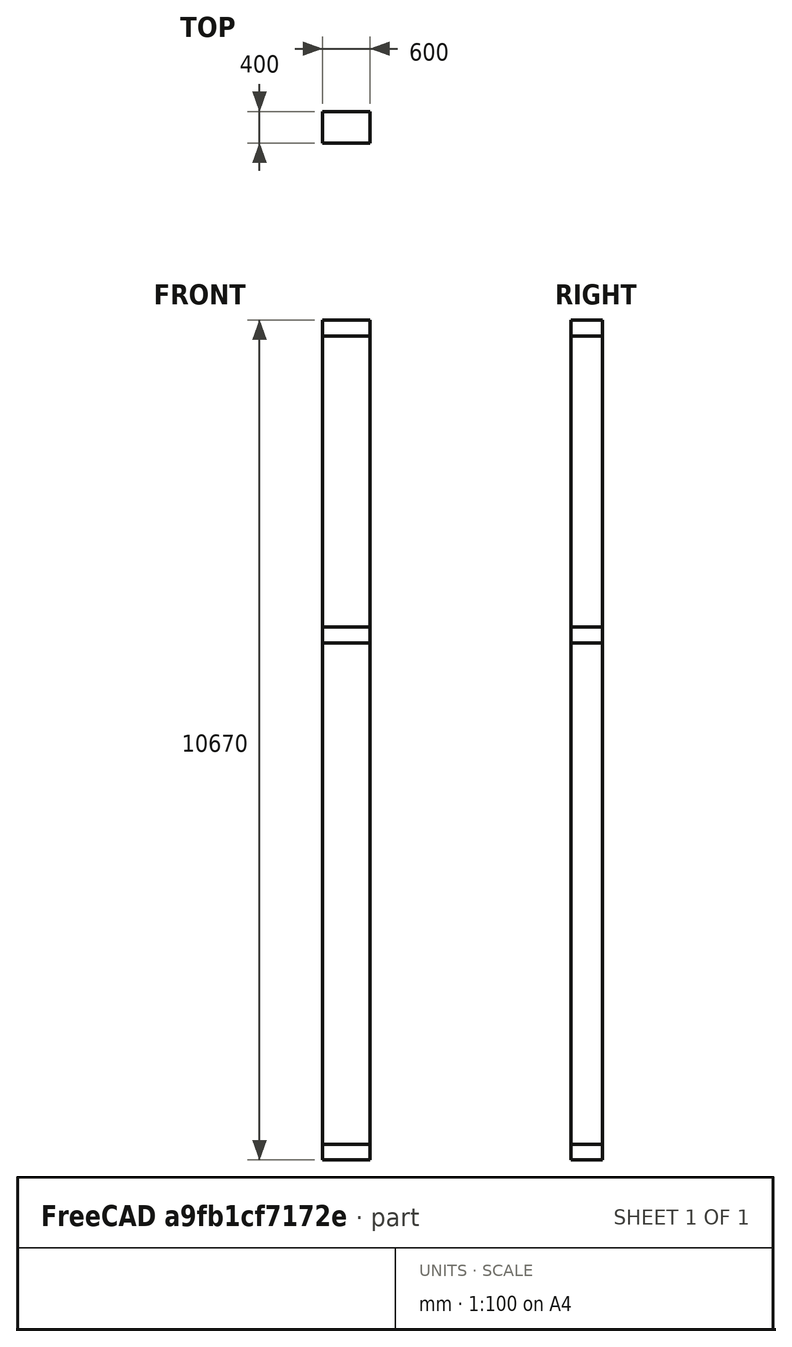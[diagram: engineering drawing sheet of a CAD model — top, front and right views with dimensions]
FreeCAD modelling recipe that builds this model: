
FCSTD DOCUMENT  (FreeCAD 0.21R33694 (Git))
Label: column
License: All rights reserved
LicenseURL: http://en.wikipedia.org/wiki/All_rights_reserved
objects: Part::FeaturePython×7, Part::Plane×5, Fem::ConstraintDisplacement×5, Part::Feature×5, Fem::ConstraintForce×4, Fem::FemSolverObjectPython×1, App::MaterialObjectPython×1, Part::Box×1, Fem::FemMeshObjectPython×1, Fem::FemAnalysis×1
note: 18 computed .brp shape members not serialized (recipe doc carries the construction recipe); baked Part::Feature solids carry a one-line shape summary decoded from their .brp

FEATURE [Fem::FemSolverObjectPython] SolverCcxTools  # FEM object (typed FeaturePython)
  AnalysisType = 0
  BeamShellResultOutput3D = true
  BucklingFactors = 1
  EigenmodeHighLimit = 1000000
  EigenmodeLowLimit = 0
  EigenmodesCount = 10
  GeometricalNonlinearity = 0
  IterationsControlParameterCutb = 0.25,0.5,0.75,0.85,,,1.5,
  IterationsControlParameterIter = 4,8,9,200,10,400,,200,,
  IterationsControlParameterTimeUse = false
  IterationsThermoMechMaximum = 2000
  IterationsUserDefinedIncrementations = false
  IterationsUserDefinedTimeStepLength = false
  MaterialNonlinearity = 0
  MatrixSolverType = 0
  SplitInputWriter = true
  ThermoMechSteadyState = true
  TimeEnd = 1
  TimeInitialStep = 0.01
FEATURE [App::MaterialObjectPython] MaterialSolid  label="B450"  # material (typed FeaturePython)
  Category = 0
  Material = AngleOfFriction=30 deg,AuthorAndLicense=(c) 2019 Bernd Hahnebach (CC-BY 3.0),CardName=Concrete-EN-C35_45,CompressiveStrength=15.75 MPa,+7 more (map truncated)
FEATURE [Part::Box] Box  label="Cube"
  AttacherType = Attacher::AttachEngine3D
  Height = 10670
  Length = 600
  Width = 400
FEATURE [Part::Plane] Plane
  AttacherType = Attacher::AttachEngine3D
  Length = 600
  Width = 400
FEATURE [Part::Plane] Plane001
  AttacherType = Attacher::AttachEngine3D
  Length = 600
  Placement = pos=(0,0,200) rot=(0,0,1;0rad)
  Width = 400
FEATURE [Part::Plane] Plane002
  AttacherType = Attacher::AttachEngine3D
  Length = 600
  Placement = pos=(0,0,6570) rot=(0,0,1;0rad)
  Width = 400
FEATURE [Part::Plane] Plane003
  AttacherType = Attacher::AttachEngine3D
  Length = 600
  Placement = pos=(0,0,6770) rot=(0,0,1;0rad)
  Width = 400
FEATURE [Part::Plane] Plane004
  AttacherType = Attacher::AttachEngine3D
  Length = 600
  Placement = pos=(0,0,10470) rot=(0,0,1;0rad)
  Width = 400
FEATURE [Part::FeaturePython] Slice  # WARN: FeaturePython — macro-defined, semantics opaque (R4)
  Base = -> Box
  Mode = 1
  Tolerance = 0
  Tools = -> [Plane,Plane001,Plane002,Plane003,Plane004]
FEATURE [Part::FeaturePython] Slice_child0  label="Slice.0"  # WARN: FeaturePython — macro-defined, semantics opaque (R4)
  Base = -> Slice
  FilterType = 1
  Invert = false
  OverrideMaxVal = 0
  WindowFrom = 80
  WindowTo = 100
  items = 0
FEATURE [Part::FeaturePython] Slice_child1  label="Slice.1"  # WARN: FeaturePython — macro-defined, semantics opaque (R4)
  Base = -> Slice
  FilterType = 1
  Invert = false
  OverrideMaxVal = 0
  WindowFrom = 80
  WindowTo = 100
  items = 1
FEATURE [Part::FeaturePython] Slice_child2  label="Slice.2"  # WARN: FeaturePython — macro-defined, semantics opaque (R4)
  Base = -> Slice
  FilterType = 1
  Invert = false
  OverrideMaxVal = 0
  WindowFrom = 80
  WindowTo = 100
  items = 2
FEATURE [Part::FeaturePython] Slice_child3  label="Slice.3"  # WARN: FeaturePython — macro-defined, semantics opaque (R4)
  Base = -> Slice
  FilterType = 1
  Invert = false
  OverrideMaxVal = 0
  WindowFrom = 80
  WindowTo = 100
  items = 3
FEATURE [Part::FeaturePython] Slice_child4  label="Slice.4"  # WARN: FeaturePython — macro-defined, semantics opaque (R4)
  Base = -> Slice
  FilterType = 1
  Invert = false
  OverrideMaxVal = 0
  WindowFrom = 80
  WindowTo = 100
  items = 4
FEATURE [Fem::ConstraintForce] ConstraintForce  label="wind"
  DirectionVector = (1,0,0)
  Force = 42000
  NormalDirection = (-1,0,0)
  Points = (136) [(0,400,0),(0,400,66.6667),(0,400,133.333),(0,400,200),(0,266.667,0),(0,266.667,66.6667),(0,266.667,133.333),(0,266.667,200),(0,133.333,0),+127 more]
  References = -> [Slice_child0,Slice_child1,Slice_child2,Slice_child3,Slice_child4]
  Reversed = true
  Scale = 19
FEATURE [Fem::ConstraintForce] ConstraintForce001  label="mast"
  DirectionVector = (1,0,0)
  Force = 10000
  NormalDirection = (-1,0,0)
  Points = (16) [(0,400,6570),(0,400,6636.67),(0,400,6703.33),(0,400,6770),(0,266.667,6570),(0,266.667,6636.67),(0,266.667,6703.33),(0,266.667,6770),(0,133.333,6570),+7 more]
  References = -> [Slice_child2]
  Reversed = true
  Scale = 19
FEATURE [Fem::ConstraintForce] ConstraintForce002  label="beam(p)"
  DirectionVector = (0,0,-1)
  Force = 100000
  NormalDirection = (0,0,1)
  Points = (16) [(0,0,10670),(200,0,10670),(400,0,10670),(600,0,10670),(0,133.333,10670),(200,133.333,10670),(400,133.333,10670),(600,133.333,10670),(0,266.667,10670),+7 more]
  References = -> [Slice_child4]
  Reversed = true
  Scale = 24
FEATURE [Fem::ConstraintDisplacement] ConstraintDisplacement  label="top_x"
  NormalDirection = (0,0,1)
  Normals = (4) [(0,0,1),(0,0,1),(0,0,1),(0,0,1)]
  Points = (4) [(600,0,10670),(600,133.333,10670),(600,266.667,10670),(600,400,10670)]
  References = -> [Slice_child4]
  Scale = 22
  hasXFormula = false
  hasYFormula = false
  hasZFormula = false
  rotxFix = false
  rotxFree = true
  rotyFix = false
  rotyFree = true
  rotzFix = false
  rotzFree = true
  useFlowSurfaceForce = false
  xDisplacement = 0
  xFix = false
  xFree = false
  xRotation = 0
  yDisplacement = 0
  yFix = false
  yFree = false
  yRotation = 0
  zDisplacement = 0
  zFix = false
  zFree = true
  zRotation = 0
FEATURE [Fem::ConstraintDisplacement] ConstraintDisplacement001  label="bottom_x"
  NormalDirection = (0,0,1)
  Normals = (4) [(0,0,1),(0,0,1),(0,0,1),(0,0,1)]
  Points = (4) [(600,0,0),(600,133.333,0),(600,266.667,0),(600,400,0)]
  References = -> [Slice_child0]
  Scale = 22
  hasXFormula = false
  hasYFormula = false
  hasZFormula = false
  rotxFix = false
  rotxFree = true
  rotyFix = false
  rotyFree = true
  rotzFix = false
  rotzFree = true
  useFlowSurfaceForce = false
  xDisplacement = 0
  xFix = false
  xFree = false
  xRotation = 0
  yDisplacement = 0
  yFix = false
  yFree = true
  yRotation = 0
  zDisplacement = 0
  zFix = false
  zFree = true
  zRotation = 0
FEATURE [Fem::ConstraintDisplacement] ConstraintDisplacement002  label="bottom_y"
  NormalDirection = (0,0,1)
  Normals = (4) [(0,0,1),(0,0,1),(0,0,1),(0,0,1)]
  Points = (4) [(0,0,0),(200,0,0),(400,0,0),(600,0,0)]
  References = -> [Slice_child0]
  Scale = 26
  hasXFormula = false
  hasYFormula = false
  hasZFormula = false
  rotxFix = false
  rotxFree = true
  rotyFix = false
  rotyFree = true
  rotzFix = false
  rotzFree = true
  useFlowSurfaceForce = false
  xDisplacement = 0
  xFix = false
  xFree = true
  xRotation = 0
  yDisplacement = 0
  yFix = false
  yFree = false
  yRotation = 0
  zDisplacement = 0
  zFix = false
  zFree = true
  zRotation = 0
FEATURE [Fem::ConstraintDisplacement] ConstraintDisplacement003  label="bottom_z"
  NormalDirection = (0,0,-1)
  Normals = (4) [(0,0,-1),(0,0,-1),(0,0,-1),(0,0,-1)]
  Points = (4) [(600,0,0),(600,133.333,0),(600,266.667,0),(600,400,0)]
  References = -> [Slice_child0]
  Scale = 22
  hasXFormula = false
  hasYFormula = false
  hasZFormula = false
  rotxFix = false
  rotxFree = true
  rotyFix = false
  rotyFree = true
  rotzFix = false
  rotzFree = true
  useFlowSurfaceForce = false
  xDisplacement = 0
  xFix = false
  xFree = true
  xRotation = 0
  yDisplacement = 0
  yFix = false
  yFree = true
  yRotation = 0
  zDisplacement = 0
  zFix = false
  zFree = false
  zRotation = 0
FEATURE [Fem::ConstraintDisplacement] ConstraintDisplacement004  label="top_y"
  NormalDirection = (0,0,1)
  Normals = (4) [(0,0,1),(0,0,1),(0,0,1),(0,0,1)]
  Points = (4) [(0,0,10670),(200,0,10670),(400,0,10670),(600,0,10670)]
  References = -> [Slice_child4]
  Scale = 26
  hasXFormula = false
  hasYFormula = false
  hasZFormula = false
  rotxFix = false
  rotxFree = true
  rotyFix = false
  rotyFree = true
  rotzFix = false
  rotzFree = true
  useFlowSurfaceForce = false
  xDisplacement = 0
  xFix = false
  xFree = true
  xRotation = 0
  yDisplacement = 0
  yFix = false
  yFree = false
  yRotation = 0
  zDisplacement = 0
  zFix = false
  zFree = true
  zRotation = 0
FEATURE [Part::Feature] Solid
  shape: bbox 600 x 400 x 200 mm, 6 faces (baked)
FEATURE [Part::Feature] Solid001
  shape: bbox 600 x 400 x 6370 mm, 6 faces (baked)
FEATURE [Part::Feature] Solid002
  shape: bbox 600 x 400 x 200 mm, 6 faces (baked)
FEATURE [Part::Feature] Solid003
  shape: bbox 600 x 400 x 3700 mm, 6 faces (baked)
FEATURE [Part::Feature] Solid004
  shape: bbox 600 x 400 x 200 mm, 6 faces (baked)
FEATURE [Part::FeaturePython] BooleanFragments  # WARN: FeaturePython — macro-defined, semantics opaque (R4)
  Mode = 2
  Objects = -> [Solid,Solid001,Solid002,Solid003,Solid004]
  Tolerance = 0
FEATURE [Fem::FemMeshObjectPython] FEMMeshGmsh  # FEM object (typed FeaturePython)
  Algorithm2D = 0
  Algorithm3D = 0
  CharacteristicLengthMax = 200
  CharacteristicLengthMin = 0
  CoherenceMesh = true
  ElementDimension = 0
  ElementOrder = 1
  GeometryTolerance = 1e-06
  GroupsOfNodes = false
  HighOrderOptimize = 0
  MeshSizeFromCurvature = 12
  OptimizeNetgen = false
  OptimizeStd = true
  Part = -> BooleanFragments
  RecombinationAlgorithm = 0
  Recombine3DAll = false
  RecombineAll = false
  SecondOrderLinear = false
FEATURE [Fem::ConstraintForce] ConstraintForce003  label="reactionz(p)"
  DirectionVector = (0,0,1)
  Force = 164020
  NormalDirection = (0,0,-1)
  Points = (16) [(0,0,0),(200,0,0),(400,0,0),(600,0,0),(0,133.333,0),(200,133.333,0),(400,133.333,0),(600,133.333,0),(0,266.667,0),(200,266.667,0),(400,266.667,0),+5 more]
  References = -> [Slice_child0]
  Reversed = true
  Scale = 24
FEATURE [Fem::FemAnalysis] Analysis
  Group = -> [SolverCcxTools,MaterialSolid,ConstraintForce,ConstraintForce001,ConstraintForce002,ConstraintDisplacement,ConstraintDisplacement001,ConstraintDisplacement002,ConstraintDisplacement003,ConstraintDisplacement004,FEMMeshGmsh,ConstraintForce003]
